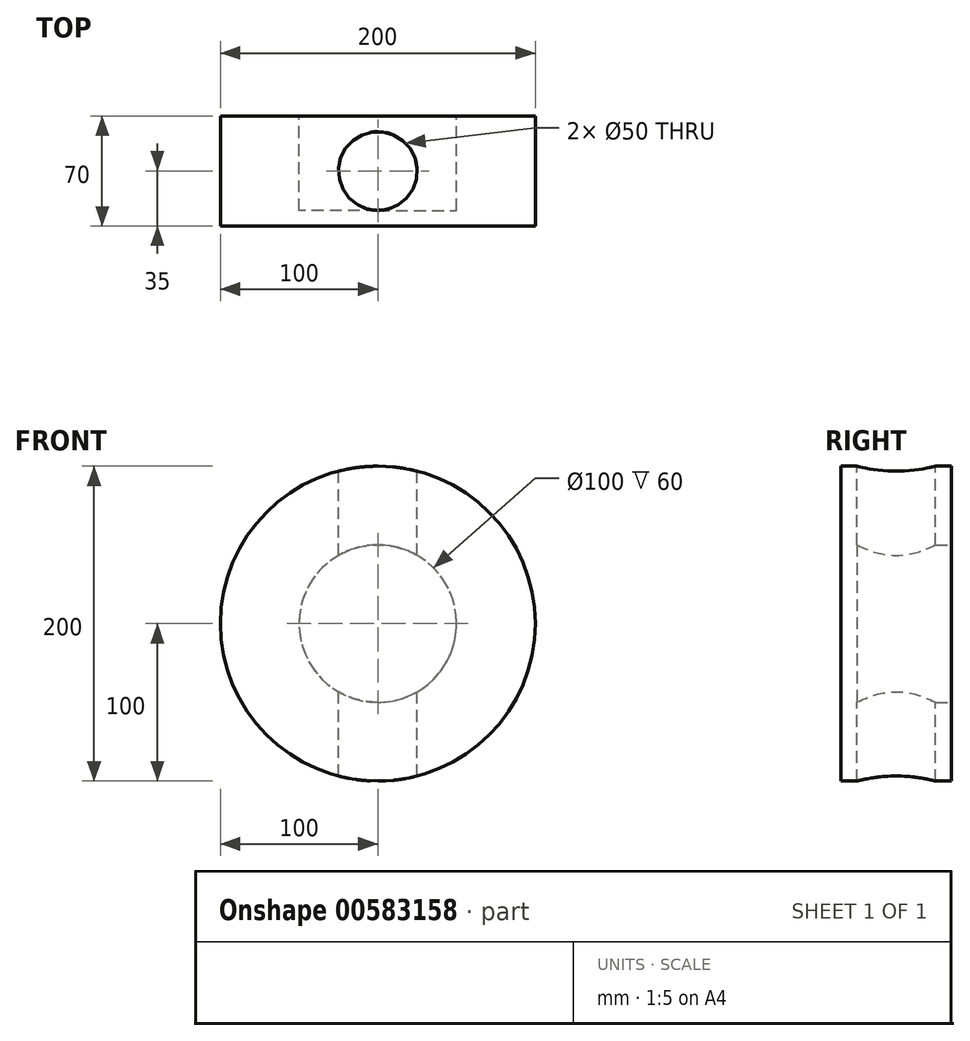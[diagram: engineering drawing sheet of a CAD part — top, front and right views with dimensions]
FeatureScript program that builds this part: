
annotation { "Feature Type Name" : "Feature", "Feature Type Description" : "" }
export const myFeature = defineFeature(function(context is Context, id is Id, definition is map)
    precondition{}
    {
        {
            var Q0;
            Q0=qCreatedBy(makeId("Front.planeOp"),FACE);
            var sketch = newSketch(context, id + "F0", { "sketchPlane" : qUnion([Q0])});
            skCircle(sketch, "E0", {"center": v(0, 0) * mm, "radius": 100 * mm});
            skCircle(sketch, "E1", {"center": v(0, 0) * mm, "radius": 50 * mm});
            skSolve(sketch);
        }
        {
            var Q0;
            Q0=makeQuery(id+"F0.imprint","IMPRINT",FACE,{"disambiguationData":[TD([[makeQuery(id+"F0.imprint","IMPRINT",EDGE,{"derivedFrom":sQuery(id+"F0.wireOp",EDGE,"E0")}),1.0]])]});
            extrude(context, id + "F1", {"entities" : qUnion([Q0]), "depth" : 60 * mm, "offsetDistance" : 25 * mm});
        }
        {
            var Q0;
            Q0=qCreatedBy(makeId("Top.planeOp"),FACE);
            var sketch = newSketch(context, id + "F2", { "sketchPlane" : qUnion([Q0])});
            skCircle(sketch, "E2", {"center": v(0, -35) * mm, "radius": 25 * mm});
            skSolve(sketch);
        }
        {
            var Q0;
            Q0=makeQuery(id+"F1.opExtrude","CAP_FACE",FACE,{"disambiguationData":[OSD([sQuery(id+"F0.wireOp",EDGE,"E0"),sQuery(id+"F0.wireOp",EDGE,"E1")])],"isStart":false});
            var sketch = newSketch(context, id + "F3", { "sketchPlane" : qUnion([Q0])});
            skCircle(sketch, "E3.0", {"center": v(0, 0) * mm, "radius": 100 * mm});
            skSolve(sketch);
        }
        {
            var Q0;
            Q0 = qSketchRegion(id + "F3", true);
            extrude(context, id + "F4", {"entities" : qUnion([Q0]), "operationType" : NewBodyOperationType.ADD, "depth" : 10 * mm, "offsetDistance" : 25 * mm});
        }
        {
            var Q0;
            Q0 = qSketchRegion(id + "F2", true);
            extrude(context, id + "F5", {"entities" : qUnion([Q0]), "operationType" : NewBodyOperationType.REMOVE, "endBound" : BoundingType.SYMMETRIC, "oppositeDirection" : true, "depth" : 308 * mm, "offsetDistance" : 25 * mm});
        }
    });
